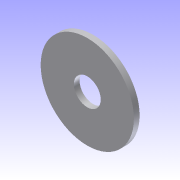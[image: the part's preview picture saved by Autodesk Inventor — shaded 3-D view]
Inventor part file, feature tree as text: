
AUTODESK INVENTOR PART (.ipt)
format: ipt  version: 2012 (Build 160160000, 160)  size: 67,584 bytes
history: native  units: in
note: dims shown in document units (in); Inventor stores cm internally (conversion verified against a paired STEP export)
features: extrude x1, sketch x1
ambient origin geometry x8: Origin, YZ Plane, XZ Plane, XY Plane, X Axis, Y Axis, Z Axis, Center Point
bodies: Solid1 (feature_tree)
feature tree (2):
  extrude  "Extrusion1"  Depth=1.005in
  sketch  "Sketch1"  dims[d0=0.29in d1=1.005in d2=0.062in d3=0.0in]
